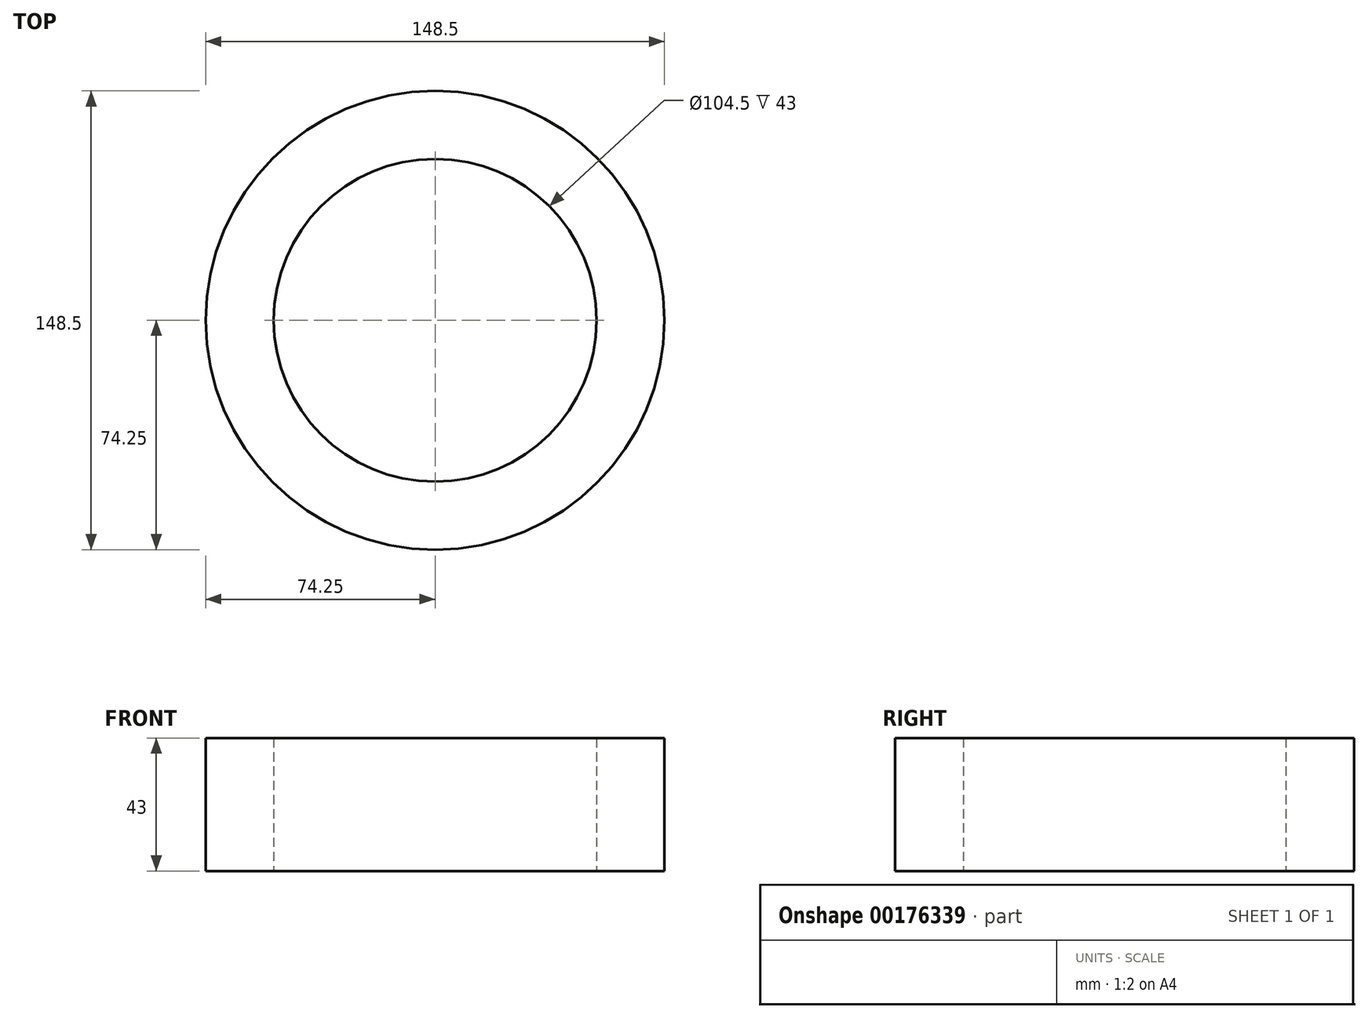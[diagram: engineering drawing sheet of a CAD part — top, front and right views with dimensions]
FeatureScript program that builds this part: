
annotation { "Feature Type Name" : "Feature", "Feature Type Description" : "" }
export const myFeature = defineFeature(function(context is Context, id is Id, definition is map)
    precondition{}
    {
        {
            var Q0;
            Q0=qCreatedBy(makeId("Top.planeOp"),FACE);
            var sketch = newSketch(context, id + "F0", { "sketchPlane" : qUnion([Q0])});
            skCircle(sketch, "E0", {"center": v(0, 0) * mm, "radius": 74.25 * mm});
            skCircle(sketch, "E1", {"center": v(0, 0) * mm, "radius": 52.25 * mm});
            skSolve(sketch);
        }
        {
            var Q0;
            Q0=makeQuery(id+"F0.imprint","IMPRINT",FACE,{"disambiguationData":[TD([[makeQuery(id+"F0.imprint","IMPRINT",EDGE,{"derivedFrom":sQuery(id+"F0.wireOp",EDGE,"E0")}),1.0]])]});
            extrude(context, id + "F1", {"entities" : qUnion([Q0]), "depth" : 43 * mm});
        }
    });
